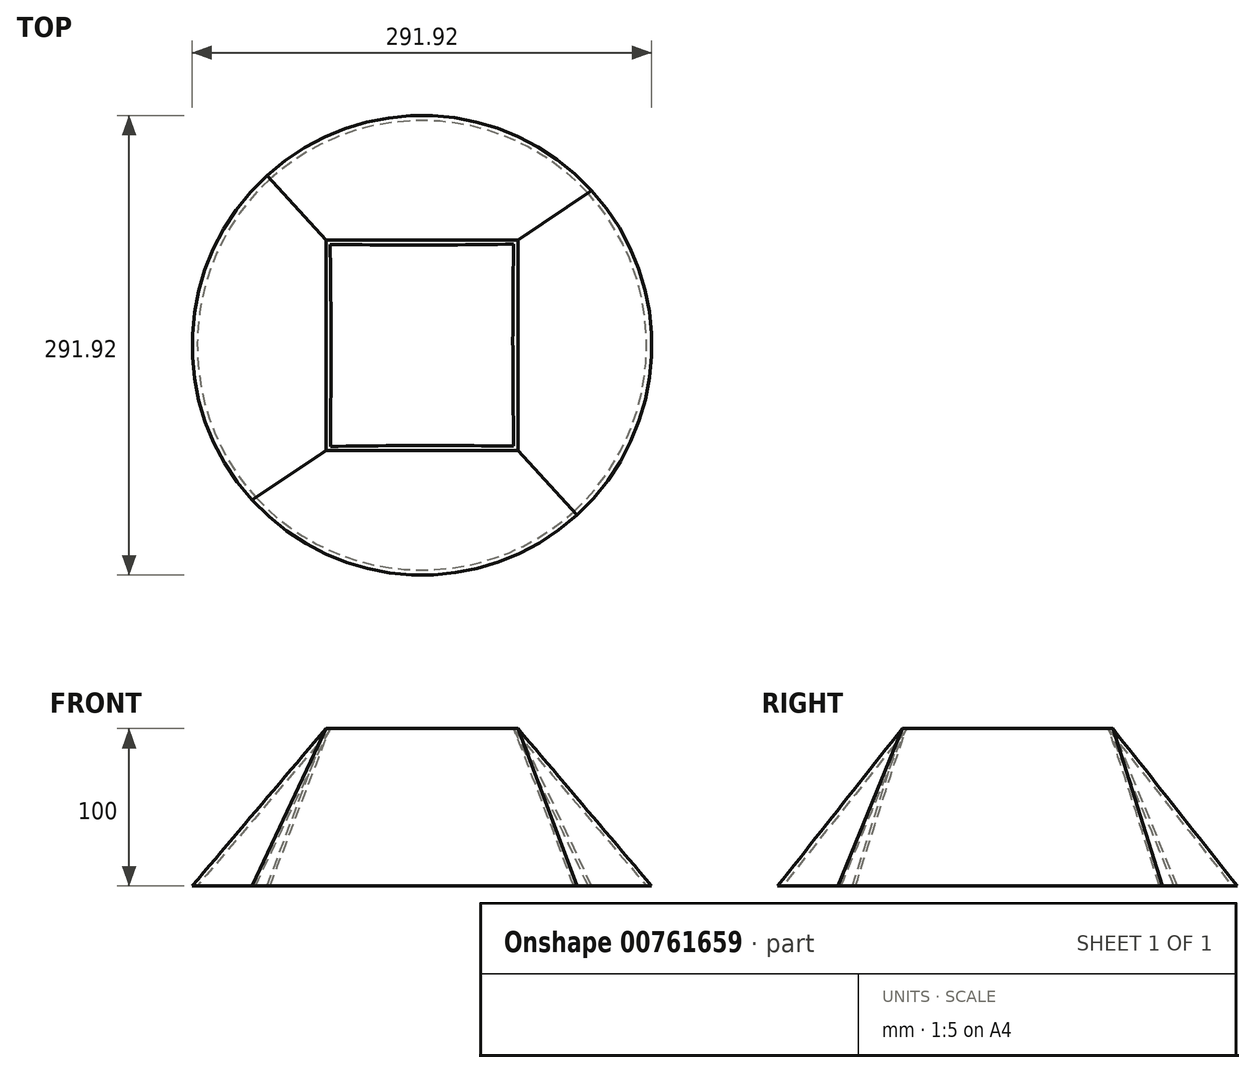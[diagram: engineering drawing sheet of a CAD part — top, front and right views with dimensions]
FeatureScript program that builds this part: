
annotation { "Feature Type Name" : "Feature", "Feature Type Description" : "" }
export const myFeature = defineFeature(function(context is Context, id is Id, definition is map)
    precondition{}
    {
        {
            var Q0;
            Q0=qCreatedBy(makeId("Top.planeOp"),FACE);
            var sketch = newSketch(context, id + "F0", { "sketchPlane" : qUnion([Q0])});
            skCircle(sketch, "E0", {"center": v(0, 0) * mm, "radius": 145.96 * mm});
            skSolve(sketch);
        }
        {
            var Q0;
            Q0=makeQuery(id+"F0.imprint","IMPRINT",FACE,{"disambiguationData":[TD([[makeQuery(id+"F0.imprint","IMPRINT",EDGE,{"derivedFrom":sQuery(id+"F0.wireOp",EDGE,"E0")}),1.0]])]});
            cPlane(context, id + "F1", {"entities" : qUnion([Q0]), "cplaneType" : CPlaneType.OFFSET, "offset" : 100 * mm, "width" : 150 * mm, "height" : 150 * mm});
        }
        {
            var Q0;
            Q0=qCreatedBy(id+"F1.planeOp",FACE);
            var sketch = newSketch(context, id + "F2", { "sketchPlane" : qUnion([Q0])});
            skLineSegment(sketch, "E1.bottom", {"start": v(60.98, -66.84) * mm, "end": v(-60.98, -66.84) * mm});
            skLineSegment(sketch, "E1.top", {"start": v(60.98, 66.84) * mm, "end": v(-60.98, 66.84) * mm});
            skLineSegment(sketch, "E1.left", {"start": v(60.98, -66.84) * mm, "end": v(60.98, 66.84) * mm});
            skLineSegment(sketch, "E1.right", {"start": v(-60.98, -66.84) * mm, "end": v(-60.98, 66.84) * mm});
            skPoint(sketch, "E1.middle", {"position": v(0, 0) * mm});
            skSolve(sketch);
        }
        {
            var Q0;
            Q0=makeQuery(id+"F0.imprint","IMPRINT",FACE,{"disambiguationData":[TD([[makeQuery(id+"F0.imprint","IMPRINT",EDGE,{"derivedFrom":sQuery(id+"F0.wireOp",EDGE,"E0")}),1.0]])]});
            var Q1;
            Q1=makeQuery(id+"F2.imprint","IMPRINT",FACE,{"disambiguationData":[TD([[makeQuery(id+"F2.imprint","IMPRINT",EDGE,{"derivedFrom":sQuery(id+"F2.wireOp",EDGE,"E1.bottom")}),-1.0]])]});
            loft(context, id + "F3", {"sheetProfilesArray" : [{ "sheetProfileEntities" : qUnion([Q0]) }, { "sheetProfileEntities" : qUnion([Q1]) }]});
        }
        {
            var Q0;
            Q0=makeQuery(id+"F3.opLoft","CAP_FACE",FACE,{"disambiguationData":[OSD([makeQuery(id+"F2.imprint","IMPRINT",FACE,{"disambiguationData":[TD([[makeQuery(id+"F2.imprint","IMPRINT",EDGE,{"derivedFrom":sQuery(id+"F2.wireOp",EDGE,"E1.bottom")}),-1.0]])]})])],"isStart":true});
            var Q1;
            Q1=makeQuery(id+"F3.opLoft","CAP_FACE",FACE,{"disambiguationData":[OSD([makeQuery(id+"F0.imprint","IMPRINT",FACE,{"disambiguationData":[TD([[makeQuery(id+"F0.imprint","IMPRINT",EDGE,{"derivedFrom":sQuery(id+"F0.wireOp",EDGE,"E0")}),1.0]])]})])],"isStart":true});
            shell(context, id + "F4", {"entities" : qUnion([Q0, Q1]), "thickness" : 2.5 * mm});
        }
    });
